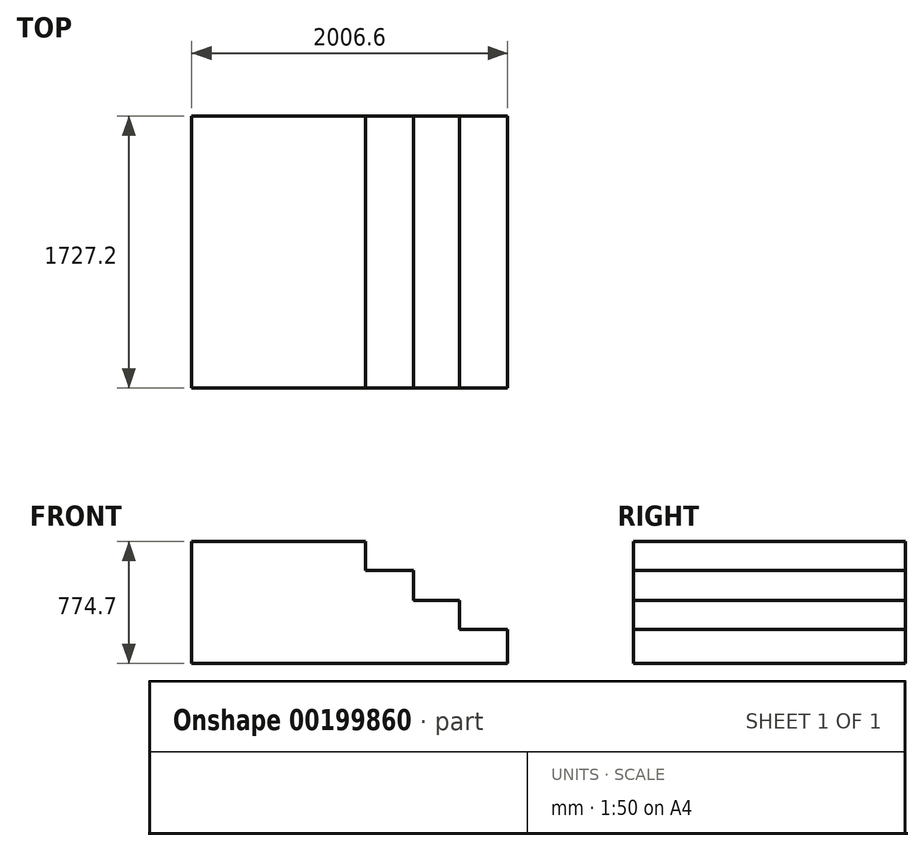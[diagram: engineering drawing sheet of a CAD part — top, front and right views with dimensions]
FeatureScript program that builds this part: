
annotation { "Feature Type Name" : "Feature", "Feature Type Description" : "" }
export const myFeature = defineFeature(function(context is Context, id is Id, definition is map)
    precondition{}
    {
        {
            var Q0;
            Q0=qCreatedBy(makeId("Front.planeOp"),FACE);
            var sketch = newSketch(context, id + "F0", { "sketchPlane" : qUnion([Q0])});
            skLineSegment(sketch, "E0", {"start": v(0, 0) * mm, "end": v(1104.9, 0) * mm});
            skLineSegment(sketch, "E1", {"start": v(1104.9, 0) * mm, "end": v(1104.9, -184.15) * mm});
            skLineSegment(sketch, "E2", {"start": v(1104.9, -184.15) * mm, "end": v(1409.7, -184.15) * mm});
            skLineSegment(sketch, "E3", {"start": v(1409.7, -184.15) * mm, "end": v(1409.7, -374.65) * mm});
            skLineSegment(sketch, "E4", {"start": v(1409.7, -374.65) * mm, "end": v(1701.8, -374.65) * mm});
            skLineSegment(sketch, "E5", {"start": v(1701.8, -374.65) * mm, "end": v(1701.8, -558.8) * mm});
            skLineSegment(sketch, "E6", {"start": v(1701.8, -558.8) * mm, "end": v(2006.6, -558.8) * mm});
            skLineSegment(sketch, "E7", {"start": v(2006.6, -558.8) * mm, "end": v(2006.6, -774.7) * mm});
            skLineSegment(sketch, "E8", {"start": v(2006.6, -774.7) * mm, "end": v(0, -774.7) * mm});
            skLineSegment(sketch, "E9", {"start": v(0, -774.7) * mm, "end": v(0, 0) * mm});
            skSolve(sketch);
        }
        {
            var Q0;
            Q0=makeQuery(id+"F0.imprint","IMPRINT",FACE,{"disambiguationData":[TD([[makeQuery(id+"F0.imprint","IMPRINT",EDGE,{"derivedFrom":sQuery(id+"F0.wireOp",EDGE,"E0")}),-1.0]])]});
            extrude(context, id + "F1", {"entities" : qUnion([Q0]), "depth" : 1727.2 * mm});
        }
    });
